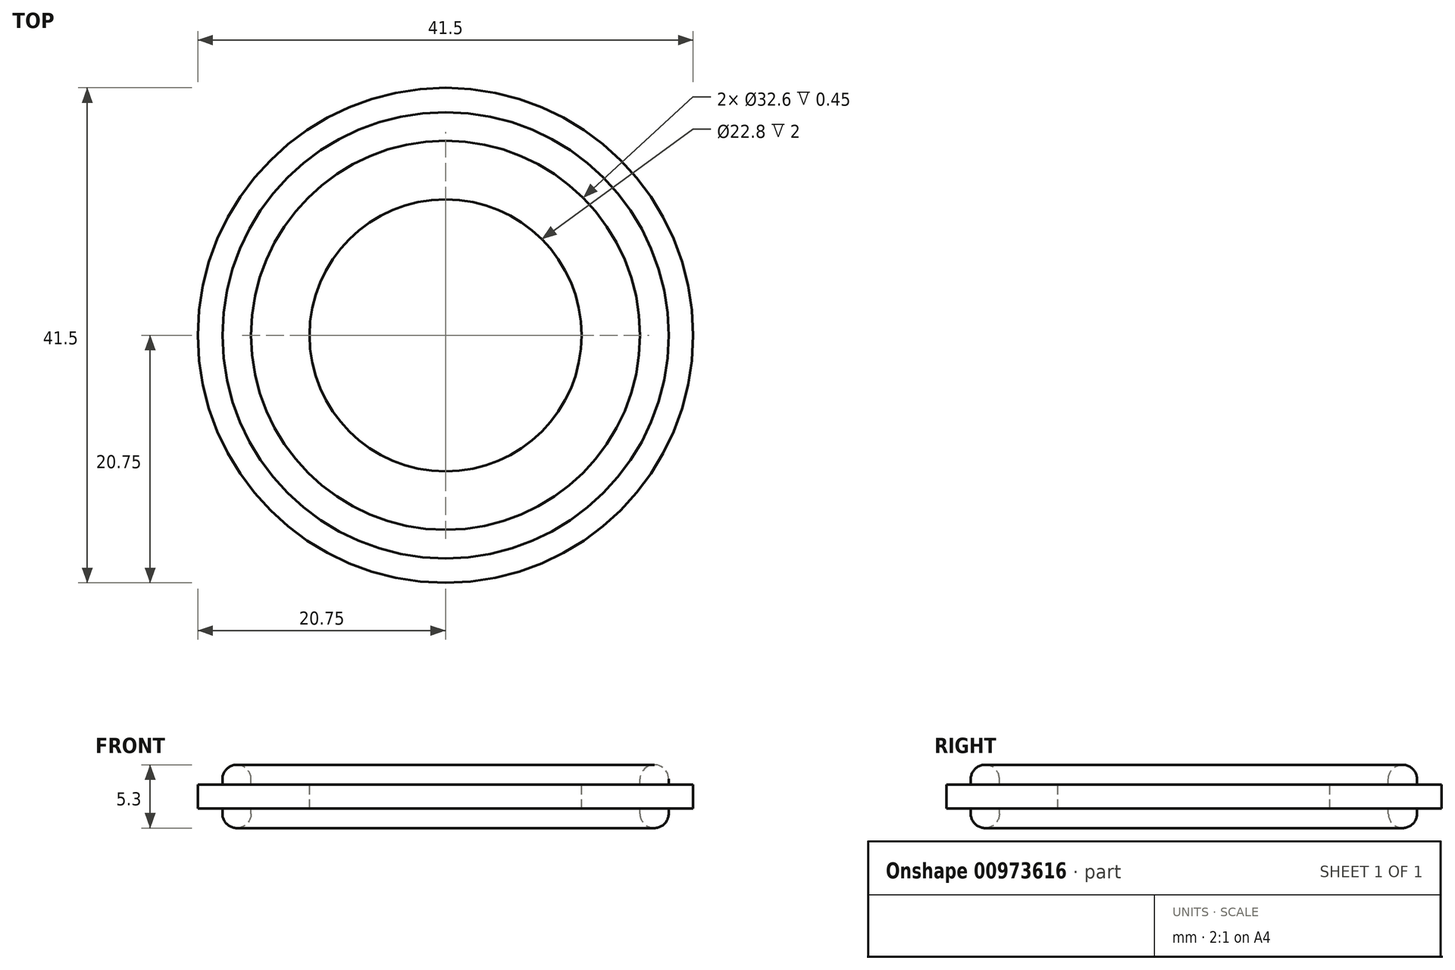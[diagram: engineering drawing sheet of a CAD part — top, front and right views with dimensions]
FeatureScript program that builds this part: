
annotation { "Feature Type Name" : "Feature", "Feature Type Description" : "" }
export const myFeature = defineFeature(function(context is Context, id is Id, definition is map)
    precondition{}
    {
        {
            var Q0;
            Q0=qCreatedBy(makeId("Front.planeOp"),FACE);
            var sketch = newSketch(context, id + "F0", { "sketchPlane" : qUnion([Q0])});
            skLineSegment(sketch, "E0.bottom", {"start": v(11.4, -1) * mm, "end": v(20.75, -1) * mm});
            skLineSegment(sketch, "E0.top", {"start": v(11.4, 1) * mm, "end": v(20.75, 1) * mm});
            skLineSegment(sketch, "E0.left", {"start": v(11.4, -1) * mm, "end": v(11.4, 1) * mm});
            skLineSegment(sketch, "E0.right", {"start": v(20.75, -1) * mm, "end": v(20.75, 1) * mm});
            skLineSegment(sketch, "E1", {"start": v(0, 0) * mm, "end": v(11.4, 0) * mm, "construction": true});
            skLineSegment(sketch, "E2", {"start": v(0, 27.06) * mm, "end": v(0, -24.1) * mm, "construction": true});
            skLineSegment(sketch, "E3.left", {"start": v(16.3, -1.45) * mm, "end": v(16.3, 1.45) * mm});
            skLineSegment(sketch, "E3.right", {"start": v(18.7, -1.45) * mm, "end": v(18.7, 1.45) * mm});
            skLineSegment(sketch, "E4", {"start": v(17.5, 1.45) * mm, "end": v(17.5, -1.45) * mm, "construction": true});
            skLineSegment(sketch, "E5", {"start": v(16.3, 0) * mm, "end": v(18.7, 0) * mm, "construction": true});
            skArc(sketch, "E6", {"start": v(18.7, 1.45) * mm, "mid": v(17.5, 2.65) * mm, "end": v(16.3, 1.45) * mm});
            skArc(sketch, "E7", {"start": v(16.3, -1.45) * mm, "mid": v(17.5, -2.65) * mm, "end": v(18.7, -1.45) * mm});
            skSolve(sketch);
        }
        {
            var Q0;
            Q0 = qSketchRegion(id + "F0", true);
            var Q1;
            Q1=sQuery(id+"F0.wireOp",EDGE,"E2");
            revolve(context, id + "F1", {"surfaceOperationType" : NewSurfaceOperationType.NEW, "entities" : qUnion([Q0]), "axis" : qUnion([Q1]), "revolveType" : RevolveType.FULL});
        }
    });
